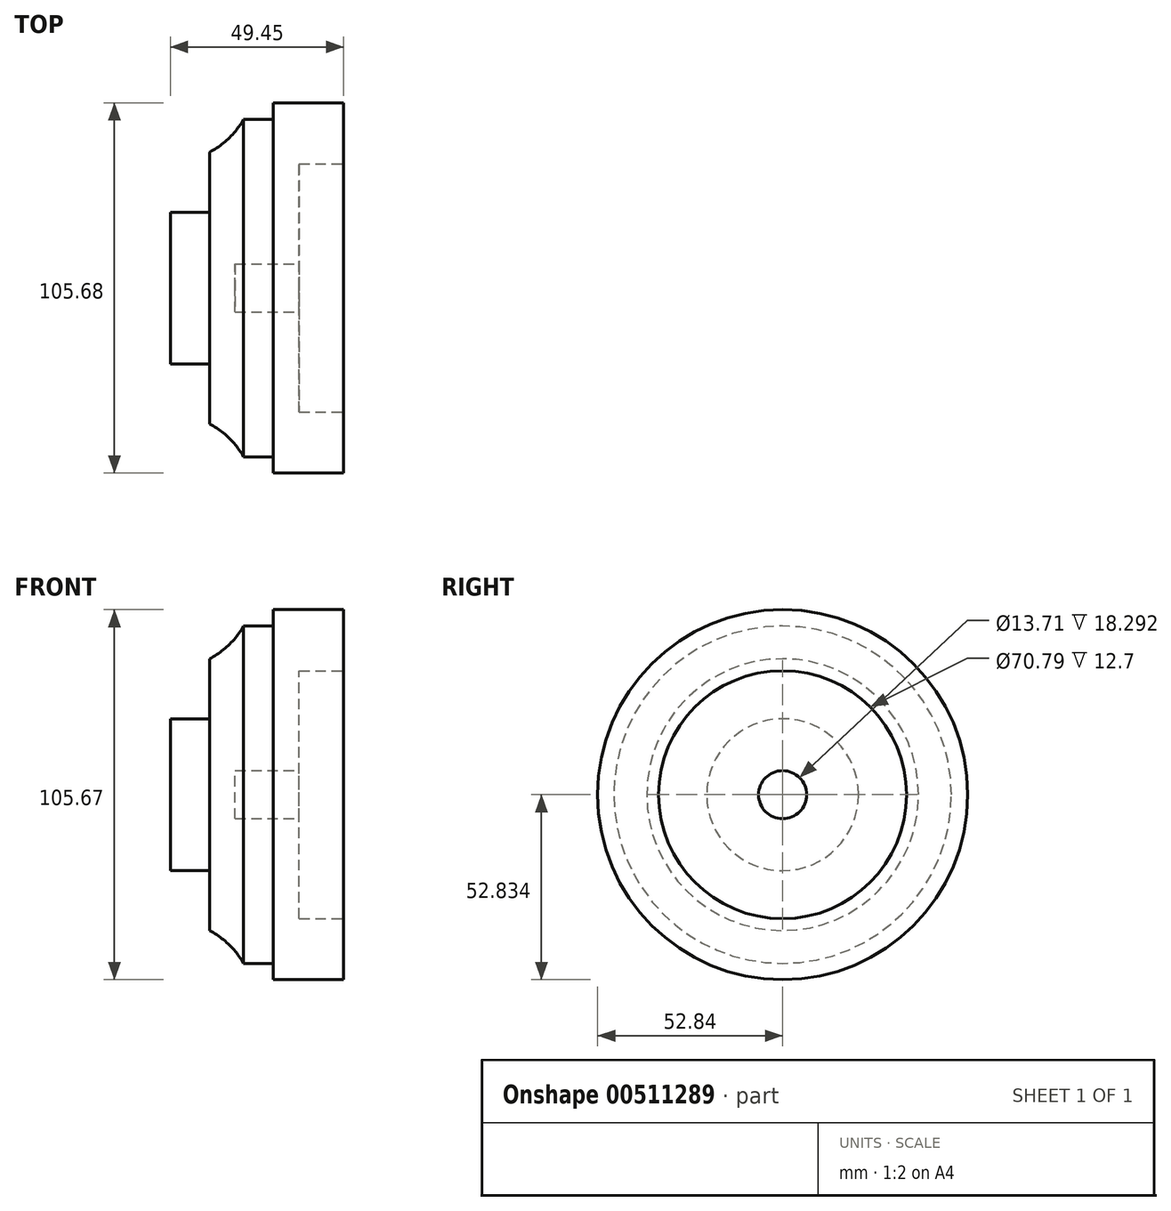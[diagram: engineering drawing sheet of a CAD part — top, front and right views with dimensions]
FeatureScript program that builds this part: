
annotation { "Feature Type Name" : "Feature", "Feature Type Description" : "" }
export const myFeature = defineFeature(function(context is Context, id is Id, definition is map)
    precondition{}
    {
        {
            var Q0;
            Q0=qCreatedBy(makeId("Front.planeOp"),FACE);
            var sketch = newSketch(context, id + "F0", { "sketchPlane" : qUnion([Q0])});
            skLineSegment(sketch, "E0.bottom", {"start": v(-2.24, 20.9) * mm, "end": v(6.18, 20.9) * mm});
            skLineSegment(sketch, "E0.top", {"start": v(-4.66, -20.41) * mm, "end": v(13.63, -20.41) * mm});
            skLineSegment(sketch, "E0.left", {"start": v(-11.98, 11.53) * mm, "end": v(-11.98, -5.59) * mm});
            skLineSegment(sketch, "E0.right", {"start": v(13.63, 8.13) * mm, "end": v(13.63, -20.41) * mm});
            skLineSegment(sketch, "E1.bottom", {"start": v(6.18, 25.57) * mm, "end": v(26.33, 25.57) * mm});
            skLineSegment(sketch, "E1.top", {"start": v(13.63, 8.13) * mm, "end": v(26.33, 8.13) * mm});
            skLineSegment(sketch, "E1.left", {"start": v(6.18, 25.57) * mm, "end": v(6.18, 20.9) * mm});
            skLineSegment(sketch, "E1.right", {"start": v(26.33, 25.57) * mm, "end": v(26.33, 8.13) * mm});
            skLineSegment(sketch, "E2.bottom", {"start": v(-4.66, -27.27) * mm, "end": v(-23.12, -27.27) * mm});
            skLineSegment(sketch, "E2.top", {"start": v(-11.98, -5.59) * mm, "end": v(-23.12, -5.59) * mm});
            skLineSegment(sketch, "E2.left", {"start": v(-4.66, -27.27) * mm, "end": v(-4.66, -20.41) * mm});
            skLineSegment(sketch, "E2.right", {"start": v(-23.12, -27.27) * mm, "end": v(-23.12, -5.59) * mm});
            skArc(sketch, "E3", {"start": v(-11.98, 11.53) * mm, "mid": v(-6.45, 15.53) * mm, "end": v(-2.24, 20.9) * mm});
            skSolve(sketch);
        }
        {
            var Q0;
            Q0=makeQuery(id+"F0.imprint","IMPRINT",FACE,{"disambiguationData":[TD([[makeQuery(id+"F0.imprint","IMPRINT",EDGE,{"derivedFrom":sQuery(id+"F0.wireOp",EDGE,"E0.bottom")}),-1.0]])]});
            var Q1;
            Q1=sQuery(id+"F0.wireOp",EDGE,"E2.bottom");
            revolve(context, id + "F1", {"entities" : qUnion([Q0]), "axis" : qUnion([Q1]), "revolveType" : RevolveType.FULL});
        }
    });
